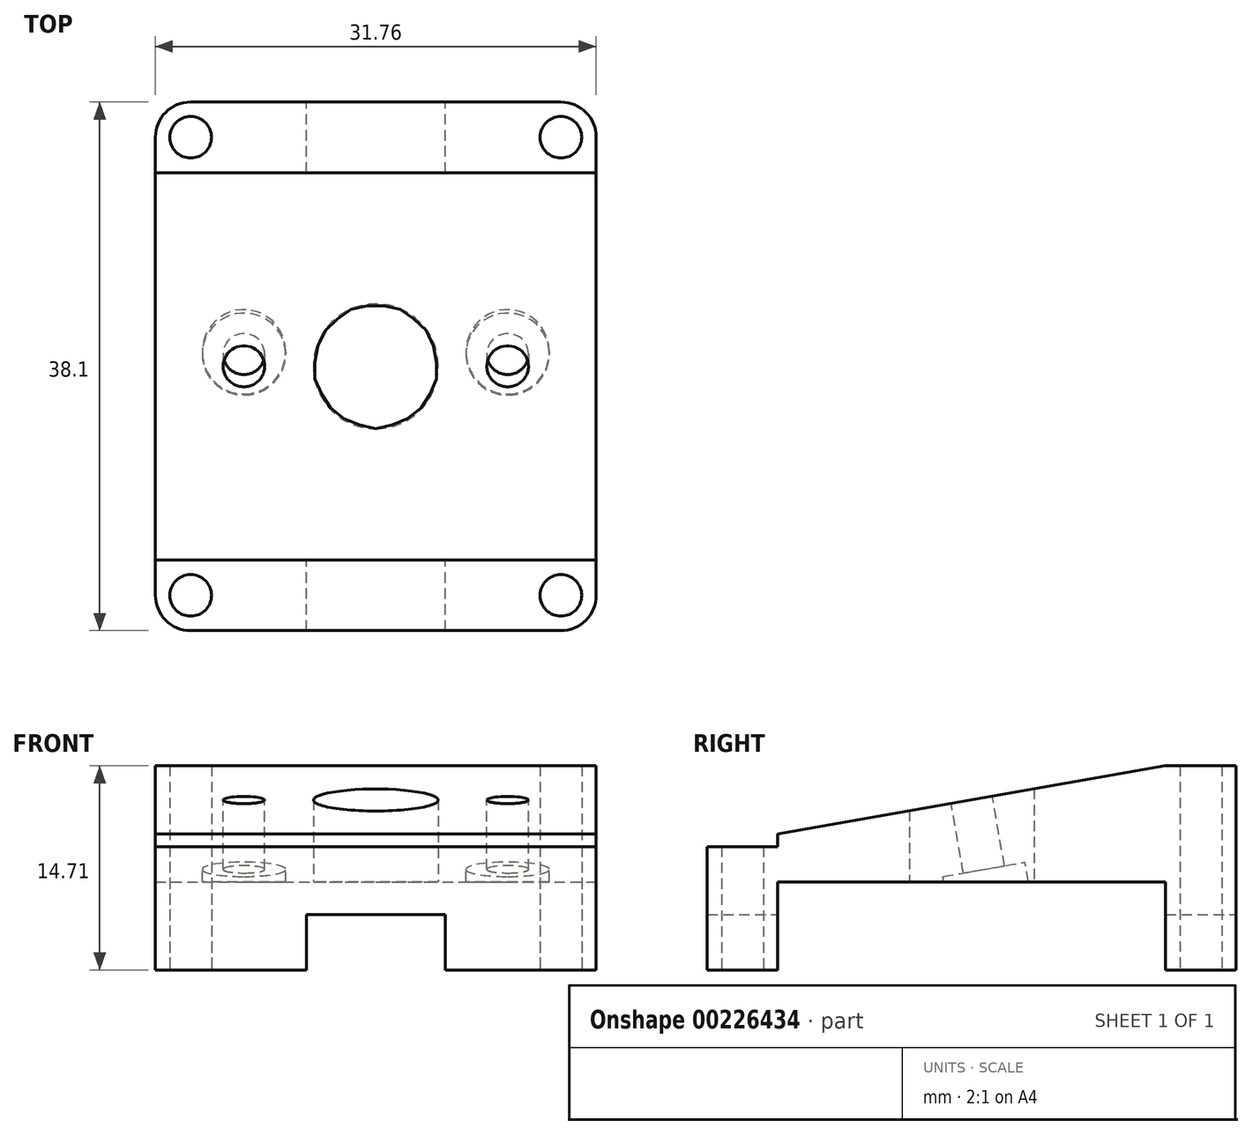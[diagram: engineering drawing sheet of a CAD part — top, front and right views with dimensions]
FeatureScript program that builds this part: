
annotation { "Feature Type Name" : "Feature", "Feature Type Description" : "" }
export const myFeature = defineFeature(function(context is Context, id is Id, definition is map)
    precondition{}
    {
        {
            var Q0;
            Q0=qCreatedBy(makeId("Top.planeOp"),FACE);
            var sketch = newSketch(context, id + "F0", { "sketchPlane" : qUnion([Q0])});
            skLineSegment(sketch, "E0.bottom", {"start": v(13.33, 19.05) * mm, "end": v(-13.34, 19.05) * mm});
            skLineSegment(sketch, "E0.top", {"start": v(13.34, -19.05) * mm, "end": v(-13.33, -19.05) * mm});
            skLineSegment(sketch, "E0.left", {"start": v(15.87, 16.51) * mm, "end": v(15.88, -16.51) * mm});
            skLineSegment(sketch, "E0.right", {"start": v(-15.88, 16.51) * mm, "end": v(-15.87, -16.51) * mm});
            skPoint(sketch, "E0.middle", {"position": v(0, 0) * mm});
            skCircle(sketch, "E1", {"center": v(0, 0) * mm, "radius": 9.5 * mm, "construction": true});
            skCircle(sketch, "E2", {"center": v(0, 0) * mm, "radius": 4.5 * mm});
            skPoint(sketch, "E3.visualSharp", {"position": v(-15.88, 19.05) * mm});
            skArc(sketch, "E3.filletArc", {"start": v(-13.34, 19.05) * mm, "mid": v(-15.13, 18.3) * mm, "end": v(-15.88, 16.51) * mm});
            skPoint(sketch, "E4.visualSharp", {"position": v(15.87, 19.05) * mm});
            skArc(sketch, "E4.filletArc", {"start": v(15.87, 16.51) * mm, "mid": v(15.13, 18.3) * mm, "end": v(13.33, 19.05) * mm});
            skPoint(sketch, "E5.visualSharp", {"position": v(15.88, -19.05) * mm});
            skArc(sketch, "E5.filletArc", {"start": v(13.34, -19.05) * mm, "mid": v(15.13, -18.3) * mm, "end": v(15.88, -16.51) * mm});
            skPoint(sketch, "E6.visualSharp", {"position": v(-15.87, -19.05) * mm});
            skArc(sketch, "E6.filletArc", {"start": v(-15.87, -16.51) * mm, "mid": v(-15.13, -18.3) * mm, "end": v(-13.33, -19.05) * mm});
            skCircle(sketch, "E7", {"center": v(-13.34, 16.51) * mm, "radius": 1.5 * mm});
            skCircle(sketch, "E8", {"center": v(13.33, 16.51) * mm, "radius": 1.5 * mm});
            skCircle(sketch, "E9", {"center": v(-13.33, -16.51) * mm, "radius": 1.5 * mm});
            skCircle(sketch, "E10", {"center": v(13.34, -16.51) * mm, "radius": 1.5 * mm});
            skCircle(sketch, "E11", {"center": v(0, 0) * mm, "radius": 13.5 * mm, "construction": true});
            skSolve(sketch);
        }
        {
            var Q0;
            Q0=makeQuery(id+"F0.imprint","IMPRINT",FACE,{"disambiguationData":[TD([[makeQuery(id+"F0.imprint","IMPRINT",EDGE,{"derivedFrom":sQuery(id+"F0.wireOp",EDGE,"E0.bottom")}),1.0]])]});
            extrude(context, id + "F1", {"entities" : qUnion([Q0]), "depth" : 2.54 * mm, "offsetDistance" : 25.4 * mm});
        }
        {
            var Q0;
            Q0=makeQuery(id+"F1.opExtrude","CAP_FACE",FACE,{"disambiguationData":[OSD([sQuery(id+"F0.wireOp",EDGE,"E0.bottom"),sQuery(id+"F0.wireOp",EDGE,"E0.top"),sQuery(id+"F0.wireOp",EDGE,"E0.left"),sQuery(id+"F0.wireOp",EDGE,"E0.right"),sQuery(id+"F0.wireOp",EDGE,"4kALpQac-FHhm-WEEX-tIft-xg5suqEFa5ex"),sQuery(id+"F0.wireOp",EDGE,"diZtlcp9-HFZ7-psaY-aWhu-X7GQ4Bjt7MnV"),sQuery(id+"F0.wireOp",EDGE,"E2"),sQuery(id+"F0.wireOp",EDGE,"E3.filletArc"),sQuery(id+"F0.wireOp",EDGE,"E4.filletArc"),sQuery(id+"F0.wireOp",EDGE,"E5.filletArc"),sQuery(id+"F0.wireOp",EDGE,"E6.filletArc"),sQuery(id+"F0.wireOp",EDGE,"E7"),sQuery(id+"F0.wireOp",EDGE,"E8"),sQuery(id+"F0.wireOp",EDGE,"E9"),sQuery(id+"F0.wireOp",EDGE,"E10")])],"isStart":true});
            var sketch = newSketch(context, id + "F2", { "sketchPlane" : qUnion([Q0])});
            skLineSegment(sketch, "E12", {"start": v(-15.87, 13.97) * mm, "end": v(15.88, 13.97) * mm});
            skLineSegment(sketch, "E13", {"start": v(15.87, -13.97) * mm, "end": v(-15.88, -13.97) * mm});
            skSolve(sketch);
        }
        {
            var Q0;
            {var subQ2=sQuery(id+"F2.wireOp",EDGE,"E12");Q0=makeQuery(id+"F2.imprint","IMPRINT",FACE,{"disambiguationData":[TD([[makeQuery(id+"F2.imprint","IMPRINT",EDGE,{"derivedFrom":subQ2}),1.0]])]});}
            var Q1;
            {var subQ3=sQuery(id+"F2.wireOp",EDGE,"E13");Q1=makeQuery(id+"F2.imprint","IMPRINT",FACE,{"disambiguationData":[TD([[makeQuery(id+"F2.imprint","IMPRINT",EDGE,{"derivedFrom":subQ3}),1.0]])]});}
            extrude(context, id + "F3", {"entities" : qUnion([Q0, Q1]), "operationType" : NewBodyOperationType.ADD, "depth" : 6.35 * mm, "offsetDistance" : 25.4 * mm});
        }
        {
            var Q0;
            {var subQ0=sQuery(id+"F0.wireOp",EDGE,"E0.bottom");Q0=makeQuery(id+"F3.boolean.opBoolean","MERGE",FACE,{"derivedFrom":[makeQuery(id+"F1.opExtrude","SWEPT_FACE",FACE,{"disambiguationData":[OSD([subQ0])]}),makeQuery(id+"F3.opExtrude","SWEPT_FACE",FACE,{"disambiguationData":[OSD([subQ0])]})]});}
            var sketch = newSketch(context, id + "F4", { "sketchPlane" : qUnion([Q0])});
            skLineSegment(sketch, "E14.bottom", {"start": v(5, -2.35) * mm, "end": v(-5, -2.35) * mm});
            skLineSegment(sketch, "E14.top", {"start": v(5, -10.35) * mm, "end": v(-5, -10.35) * mm});
            skLineSegment(sketch, "E14.left", {"start": v(5, -2.35) * mm, "end": v(5, -10.35) * mm});
            skLineSegment(sketch, "E14.right", {"start": v(-5, -2.35) * mm, "end": v(-5, -10.35) * mm});
            skPoint(sketch, "E14.middle", {"position": v(0, -6.35) * mm});
            skSolve(sketch);
        }
        {
            var Q0;
            {var subQ0=sQuery(id+"F4.wireOp",EDGE,"E14.bottom");Q0=makeQuery(id+"F4.imprint","IMPRINT",FACE,{"disambiguationData":[TD([[makeQuery(id+"F4.imprint","IMPRINT",EDGE,{"derivedFrom":subQ0}),1.0]])]});}
            extrude(context, id + "F5", {"entities" : qUnion([Q0]), "operationType" : NewBodyOperationType.REMOVE, "endBound" : BoundingType.THROUGH_ALL, "oppositeDirection" : true, "depth" : 25.4 * mm, "offsetDistance" : 25.4 * mm});
        }
        {
            var Q0;
            Q0=makeQuery(id+"F1.opExtrude","CAP_EDGE",EDGE,{"disambiguationData":[OSD([sQuery(id+"F0.wireOp",EDGE,"E0.top")])],"isStart":false});
            cPlane(context, id + "F6", {"entities" : qUnion([Q0]), "cplaneType" : CPlaneType.LINE_ANGLE, "offset" : 25.4 * mm, "angle" : 80 * degree, "width" : 152.4 * mm, "height" : 152.4 * mm});
        }
        {
            var Q0;
            Q0=makeQuery(id+"F1.opExtrude","CAP_FACE",FACE,{"disambiguationData":[OSD([sQuery(id+"F0.wireOp",EDGE,"E0.bottom"),sQuery(id+"F0.wireOp",EDGE,"E0.top"),sQuery(id+"F0.wireOp",EDGE,"E0.left"),sQuery(id+"F0.wireOp",EDGE,"E0.right"),sQuery(id+"F0.wireOp",EDGE,"4kALpQac-FHhm-WEEX-tIft-xg5suqEFa5ex"),sQuery(id+"F0.wireOp",EDGE,"diZtlcp9-HFZ7-psaY-aWhu-X7GQ4Bjt7MnV"),sQuery(id+"F0.wireOp",EDGE,"E2"),sQuery(id+"F0.wireOp",EDGE,"E3.filletArc"),sQuery(id+"F0.wireOp",EDGE,"E4.filletArc"),sQuery(id+"F0.wireOp",EDGE,"E5.filletArc"),sQuery(id+"F0.wireOp",EDGE,"E6.filletArc"),sQuery(id+"F0.wireOp",EDGE,"E7"),sQuery(id+"F0.wireOp",EDGE,"E8"),sQuery(id+"F0.wireOp",EDGE,"E9"),sQuery(id+"F0.wireOp",EDGE,"E10")])],"isStart":false});
            extrude(context, id + "F7", {"entities" : qUnion([Q0]), "operationType" : NewBodyOperationType.ADD, "depth" : 25.4 * mm, "offsetDistance" : 25.4 * mm});
        }
        {
            var Q0;
            Q0=qCreatedBy(id+"F6.planeOp",FACE);
            var sketch = newSketch(context, id + "F8", { "sketchPlane" : qUnion([Q0])});
            skLineSegment(sketch, "E15.bottom", {"start": v(-20.94, 43.45) * mm, "end": v(30.1, 43.45) * mm});
            skLineSegment(sketch, "E15.top", {"start": v(-20.94, -32.48) * mm, "end": v(30.1, -32.48) * mm});
            skLineSegment(sketch, "E15.left", {"start": v(-20.94, 43.45) * mm, "end": v(-20.94, -32.48) * mm});
            skLineSegment(sketch, "E15.right", {"start": v(30.1, 43.45) * mm, "end": v(30.1, -32.48) * mm});
            skSolve(sketch);
        }
        {
            var Q0;
            Q0=makeQuery(id+"F8.imprint","IMPRINT",FACE,{"disambiguationData":[TD([[makeQuery(id+"F8.imprint","IMPRINT",EDGE,{"derivedFrom":sQuery(id+"F8.wireOp",EDGE,"E15.bottom")}),-1.0]])]});
            extrude(context, id + "F9", {"entities" : qUnion([Q0]), "operationType" : NewBodyOperationType.REMOVE, "depth" : 25.4 * mm, "offsetDistance" : 25.4 * mm});
        }
        {
            var Q0;
            {var subQ0=sQuery(id+"F0.wireOp",EDGE,"E4.filletArc");var subQ1=sQuery(id+"F0.wireOp",EDGE,"E0.left");var subQ3=sQuery(id+"F2.wireOp",EDGE,"E13");var subQ4=sQuery(id+"F0.wireOp",EDGE,"E8");var subQ5=sQuery(id+"F0.wireOp",EDGE,"E0.bottom");Q0=makeQuery(id+"F5.boolean.opBoolean","SPLIT",FACE,{"disambiguationData":[TD([makeQuery(id+"F1.opExtrude","SWEPT_FACE",FACE,{"disambiguationData":[OSD([subQ1])]})])],"derivedFrom":makeQuery(id+"F3.opExtrude","CAP_FACE",FACE,{"disambiguationData":[OSD([subQ5,subQ1,sQuery(id+"F0.wireOp",EDGE,"E0.right"),sQuery(id+"F0.wireOp",EDGE,"E3.filletArc"),subQ0,sQuery(id+"F0.wireOp",EDGE,"E7"),subQ4,subQ3])],"isStart":false})});}
            cPlane(context, id + "F10", {"entities" : qUnion([Q0]), "cplaneType" : CPlaneType.OFFSET, "offset" : 14.7 * mm, "oppositeDirection" : true, "width" : 152.4 * mm, "height" : 152.4 * mm});
        }
        {
            var Q0;
            Q0=qCreatedBy(id+"F10.planeOp",FACE);
            var sketch = newSketch(context, id + "F11", { "sketchPlane" : qUnion([Q0])});
            skLineSegment(sketch, "E16.bottom", {"start": v(-20.95, -22.73) * mm, "end": v(29.76, -22.73) * mm});
            skLineSegment(sketch, "E16.top", {"start": v(-20.95, -7.27) * mm, "end": v(29.76, -7.27) * mm});
            skLineSegment(sketch, "E16.left", {"start": v(-20.95, -22.73) * mm, "end": v(-20.95, -7.27) * mm});
            skLineSegment(sketch, "E16.right", {"start": v(29.76, -22.73) * mm, "end": v(29.76, -7.27) * mm});
            skSolve(sketch);
        }
        {
            var Q0;
            Q0=makeQuery(id+"F11.imprint","IMPRINT",FACE,{"disambiguationData":[TD([[makeQuery(id+"F11.imprint","IMPRINT",EDGE,{"derivedFrom":sQuery(id+"F11.wireOp",EDGE,"E16.bottom")}),1.0]])]});
            extrude(context, id + "F12", {"entities" : qUnion([Q0]), "operationType" : NewBodyOperationType.REMOVE, "oppositeDirection" : true, "depth" : 25.4 * mm, "offsetDistance" : 25.4 * mm});
        }
        {
            var Q0;
            {var subQ0=sQuery(id+"F0.wireOp",EDGE,"E5.filletArc");var subQ1=sQuery(id+"F0.wireOp",EDGE,"E0.left");var subQ3=sQuery(id+"F2.wireOp",EDGE,"E12");var subQ4=sQuery(id+"F0.wireOp",EDGE,"E10");var subQ5=sQuery(id+"F0.wireOp",EDGE,"E0.top");Q0=makeQuery(id+"F5.boolean.opBoolean","SPLIT",FACE,{"disambiguationData":[TD([makeQuery(id+"F1.opExtrude","SWEPT_FACE",FACE,{"disambiguationData":[OSD([subQ1])]})])],"derivedFrom":makeQuery(id+"F3.opExtrude","CAP_FACE",FACE,{"disambiguationData":[OSD([subQ5,subQ1,sQuery(id+"F0.wireOp",EDGE,"E0.right"),subQ0,sQuery(id+"F0.wireOp",EDGE,"E6.filletArc"),sQuery(id+"F0.wireOp",EDGE,"E9"),subQ4,subQ3])],"isStart":false})});}
            cPlane(context, id + "F13", {"entities" : qUnion([Q0]), "cplaneType" : CPlaneType.OFFSET, "offset" : 8.9 * mm, "oppositeDirection" : true, "width" : 152.4 * mm, "height" : 152.4 * mm});
        }
        {
            var Q0;
            Q0=qCreatedBy(id+"F13.planeOp",FACE);
            var sketch = newSketch(context, id + "F14", { "sketchPlane" : qUnion([Q0])});
            skLineSegment(sketch, "E17.bottom", {"start": v(23.07, 19.05) * mm, "end": v(-22.22, 19.05) * mm});
            skLineSegment(sketch, "E17.top", {"start": v(23.07, 13.97) * mm, "end": v(-22.22, 13.97) * mm});
            skLineSegment(sketch, "E17.left", {"start": v(23.07, 19.05) * mm, "end": v(23.07, 13.97) * mm});
            skLineSegment(sketch, "E17.right", {"start": v(-22.22, 19.05) * mm, "end": v(-22.22, 13.97) * mm});
            skSolve(sketch);
        }
        {
            var Q0;
            Q0=makeQuery(id+"F14.imprint","IMPRINT",FACE,{"disambiguationData":[TD([[makeQuery(id+"F14.imprint","IMPRINT",EDGE,{"derivedFrom":sQuery(id+"F14.wireOp",EDGE,"E17.bottom")}),1.0]])]});
            extrude(context, id + "F15", {"entities" : qUnion([Q0]), "operationType" : NewBodyOperationType.REMOVE, "oppositeDirection" : true, "depth" : 25.4 * mm, "offsetDistance" : 25.4 * mm});
        }
        {
            var Q0;
            Q0=makeQuery(id+"F9.boolean.opBoolean","COPY",FACE,{"derivedFrom":makeQuery(id+"F9.opExtrude","CAP_FACE",FACE,{"disambiguationData":[OSD([sQuery(id+"F8.wireOp",EDGE,"E15.bottom"),sQuery(id+"F8.wireOp",EDGE,"E15.top"),sQuery(id+"F8.wireOp",EDGE,"E15.left"),sQuery(id+"F8.wireOp",EDGE,"E15.right")])],"isStart":true})});
            var sketch = newSketch(context, id + "F16", { "sketchPlane" : qUnion([Q0])});
            skEllipse(sketch, "E18.0", {"center": v(0, 1.02) * mm, "majorRadius": 4.57 * mm, "minorRadius": 4.5 * mm, "majorAxis": v(0, -1)});
            skLineSegment(sketch, "E19", {"start": v(9.5, 1.02) * mm, "end": v(-9.5, 1.02) * mm});
            skCircle(sketch, "E20", {"center": v(9.5, 1.02) * mm, "radius": 1.5 * mm});
            skCircle(sketch, "E21", {"center": v(-9.5, 1.02) * mm, "radius": 1.5 * mm});
            skSolve(sketch);
        }
        {
            var Q0;
            Q0=makeQuery(id+"F16.imprint","IMPRINT",FACE,{"disambiguationData":[TD([[makeQuery(id+"F16.imprint","IMPRINT",EDGE,{"derivedFrom":sQuery(id+"F16.wireOp",EDGE,"E21")}),1.0]])]});
            var Q1;
            Q1=makeQuery(id+"F16.imprint","IMPRINT",FACE,{"disambiguationData":[TD([[makeQuery(id+"F16.imprint","IMPRINT",EDGE,{"derivedFrom":sQuery(id+"F16.wireOp",EDGE,"E20")}),1.0]])]});
            extrude(context, id + "F17", {"entities" : qUnion([Q0, Q1]), "operationType" : NewBodyOperationType.REMOVE, "oppositeDirection" : true, "depth" : 25.4 * mm, "offsetDistance" : 25.4 * mm});
        }
        {
            var Q0;
            Q0=makeQuery(id+"F9.boolean.opBoolean","COPY",FACE,{"derivedFrom":makeQuery(id+"F9.opExtrude","CAP_FACE",FACE,{"disambiguationData":[OSD([sQuery(id+"F8.wireOp",EDGE,"E15.bottom"),sQuery(id+"F8.wireOp",EDGE,"E15.top"),sQuery(id+"F8.wireOp",EDGE,"E15.left"),sQuery(id+"F8.wireOp",EDGE,"E15.right")])],"isStart":true})});
            cPlane(context, id + "F18", {"entities" : qUnion([Q0]), "cplaneType" : CPlaneType.OFFSET, "offset" : 5.08 * mm, "oppositeDirection" : true, "width" : 152.4 * mm, "height" : 152.4 * mm});
        }
        {
            var Q0;
            Q0=qCreatedBy(id+"F18.planeOp",FACE);
            var sketch = newSketch(context, id + "F19", { "sketchPlane" : qUnion([Q0])});
            skCircle(sketch, "E22.0", {"center": v(9.5, 1.02) * mm, "radius": 1.5 * mm});
            skCircle(sketch, "E22.1", {"center": v(-9.5, 1.02) * mm, "radius": 1.5 * mm});
            skCircle(sketch, "E23", {"center": v(9.5, 1.02) * mm, "radius": 3 * mm});
            skCircle(sketch, "E24", {"center": v(-9.5, 1.02) * mm, "radius": 3 * mm});
            skSolve(sketch);
        }
        {
            var Q0;
            Q0 = qSketchRegion(id + "F19", true);
            extrude(context, id + "F20", {"entities" : qUnion([Q0]), "operationType" : NewBodyOperationType.REMOVE, "oppositeDirection" : true, "depth" : 25.4 * mm, "offsetDistance" : 25.4 * mm});
        }
    });
